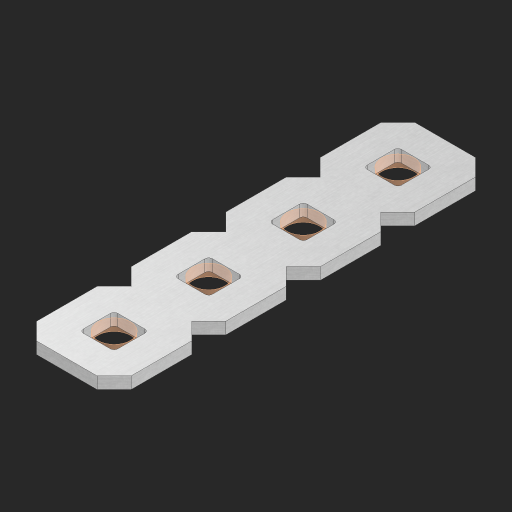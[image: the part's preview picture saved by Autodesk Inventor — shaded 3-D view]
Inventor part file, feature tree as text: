
AUTODESK INVENTOR PART (.ipt)
format: ipt  version: 2023 (Build 270158000, 158)  size: 314,880 bytes
history: native  units: in
note: dims shown in document units (in); Inventor stores cm internally (conversion verified against a paired STEP export)
features: other x5, extrude x3, sketch x2, pattern_linear x1
ambient origin geometry x8: Origin, YZ Plane, XZ Plane, XY Plane, X Axis, Y Axis, Z Axis, Center Point
bodies: Solid1 (feature_tree), Body (feature_tree)
feature tree (11):
  pattern_linear  "Rectangular Pattern1"  Spacing1=0.09in  [1 undecoded]
  sketch  "Sketch1"  dims[d1=0.5in]
  sketch  "Sketch2"  dims[d2=0.182in d3=0.09in d4=0.09in d5=0.09in d6=0.09in d7=0.09in d8=0.09in d9=0.09in d10=0.09in d11=0.02in d13=0.0in d14=0.172in d15=0.0625in d16=0.0in d19=0.5in d22=0.5in]
  other  "Srf1"
  other  "Srf126"
  other  "Srf127"
  other  "Srf128"
  other  "Circle"
  extrude  "ExtrusionSrf126"  Depth=0.09in
  extrude  "ExtrusionSrf127"  Depth=0.09in
  extrude  "ExtrusionSrf128"  Depth=0.09in
note: 1 required parameter value undecoded (feature->parameter linkage not recoverable at this tier; creation-order binding heuristic only, values carry confidence <= 0.55)
